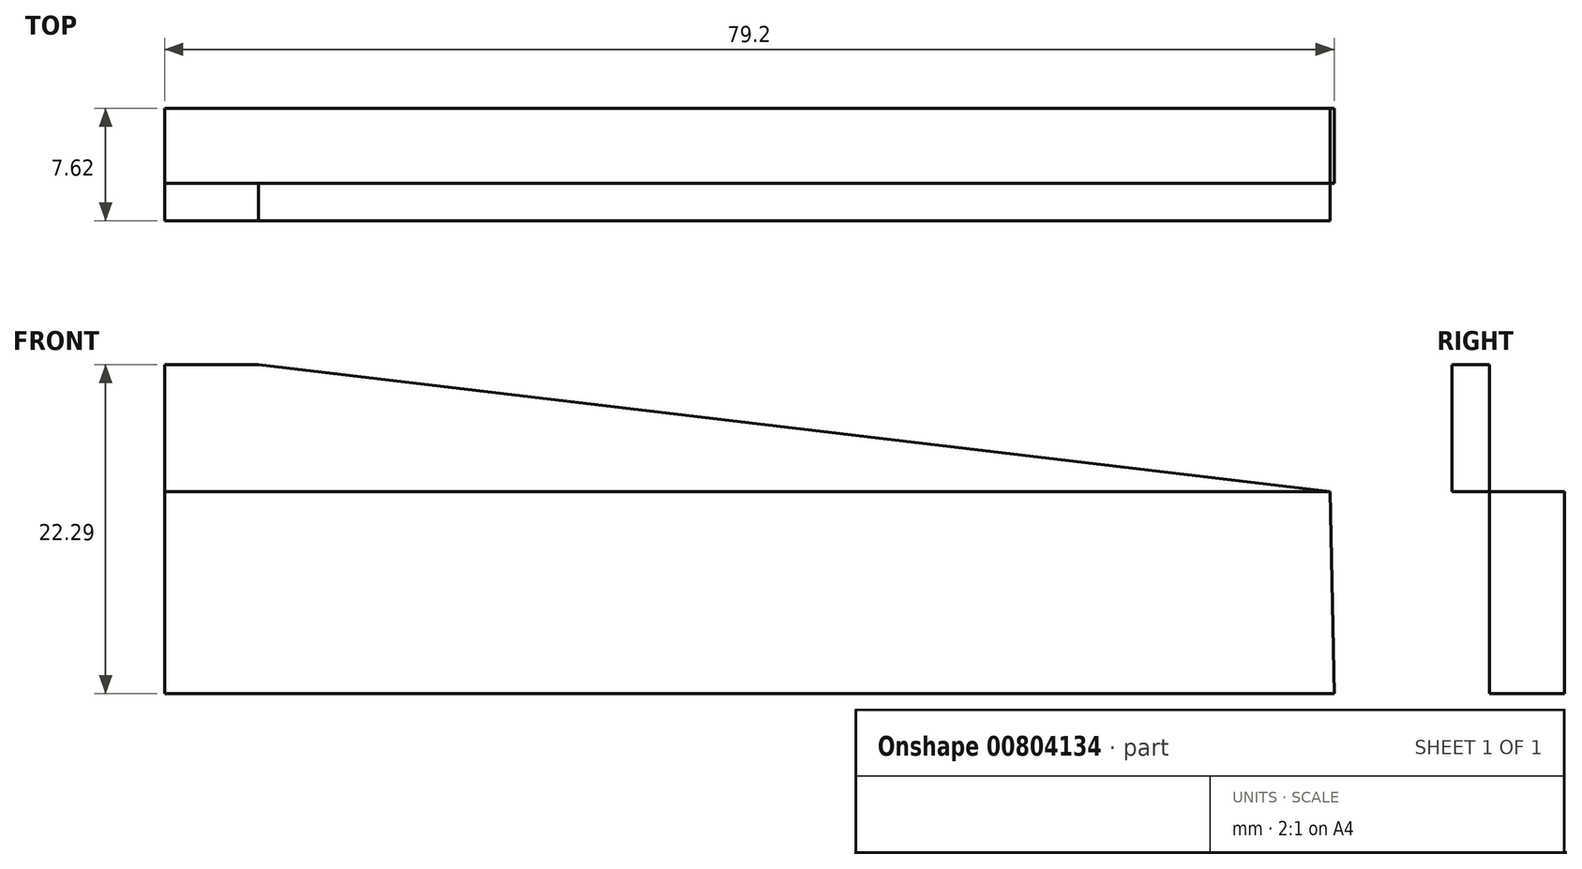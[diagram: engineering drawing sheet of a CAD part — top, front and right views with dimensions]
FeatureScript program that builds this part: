
annotation { "Feature Type Name" : "Feature", "Feature Type Description" : "" }
export const myFeature = defineFeature(function(context is Context, id is Id, definition is map)
    precondition{}
    {
        {
            var Q0;
            Q0=qCreatedBy(makeId("Front.planeOp"),FACE);
            var sketch = newSketch(context, id + "F0", { "sketchPlane" : qUnion([Q0])});
            skLineSegment(sketch, "E0", {"start": v(-14.36, 7.65) * mm, "end": v(64.84, 7.65) * mm});
            skLineSegment(sketch, "E1", {"start": v(-14.36, 7.65) * mm, "end": v(-14.36, 21.34) * mm});
            skLineSegment(sketch, "E2", {"start": v(-14.36, 21.34) * mm, "end": v(64.57, 21.34) * mm});
            skLineSegment(sketch, "E3", {"start": v(64.57, 21.34) * mm, "end": v(64.84, 7.65) * mm});
            skSolve(sketch);
        }
        {
            var Q0;
            Q0 = qSketchRegion(id + "F0", true);
            var Q1;
            Q1=makeQuery(id+"F0.imprint","IMPRINT",FACE,{"disambiguationData":[TD([[makeQuery(id+"F0.imprint","IMPRINT",EDGE,{"derivedFrom":sQuery(id+"F0.wireOp",EDGE,"E0")}),1.0]])]});
            extrude(context, id + "F1", {"entities" : qUnion([Q0, Q1]), "depth" : 2.54 * mm, "offsetDistance" : 25.4 * mm});
        }
        {
            var Q0;
            Q0=qCreatedBy(makeId("Right.planeOp"),FACE);
            var sketch = newSketch(context, id + "F2", { "sketchPlane" : qUnion([Q0])});
            skSolve(sketch);
        }
        {
            var Q0;
            Q0 = qSketchRegion(id + "F2", true);
            var Q1;
            Q1=makeQuery(id+"F1.opExtrude","CAP_FACE",FACE,{"disambiguationData":[OSD([sQuery(id+"F0.wireOp",EDGE,"E0"),sQuery(id+"F0.wireOp",EDGE,"E1"),sQuery(id+"F0.wireOp",EDGE,"E2"),sQuery(id+"F0.wireOp",EDGE,"E3")])],"isStart":false});
            extrude(context, id + "F3", {"entities" : qUnion([Q0, Q1]), "operationType" : NewBodyOperationType.ADD, "depth" : 2.54 * mm, "offsetDistance" : 25.4 * mm});
        }
        {
            var Q0;
            Q0=makeQuery(id+"F3.opExtrude","CAP_FACE",FACE,{"disambiguationData":[OSD([sQuery(id+"F0.wireOp",EDGE,"E0"),sQuery(id+"F0.wireOp",EDGE,"E1"),sQuery(id+"F0.wireOp",EDGE,"E2"),sQuery(id+"F0.wireOp",EDGE,"E3")])],"isStart":false});
            var sketch = newSketch(context, id + "F4", { "sketchPlane" : qUnion([Q0])});
            skLineSegment(sketch, "E4", {"start": v(-14.36, 21.34) * mm, "end": v(-14.36, 29.94) * mm});
            skLineSegment(sketch, "E5", {"start": v(-14.36, 29.94) * mm, "end": v(-8.01, 29.94) * mm});
            skLineSegment(sketch, "E6", {"start": v(-8.01, 29.94) * mm, "end": v(64.57, 21.34) * mm});
            skSolve(sketch);
        }
        {
            var Q0;
            Q0=makeQuery(id+"F4.imprint","IMPRINT",FACE,{"disambiguationData":[TD([[makeQuery(id+"F4.imprint","IMPRINT",EDGE,{"derivedFrom":sQuery(id+"F4.wireOp",EDGE,"E4")}),-1.0]])]});
            extrude(context, id + "F5", {"entities" : qUnion([Q0]), "depth" : 2.54 * mm, "offsetDistance" : 25.4 * mm});
        }
    });
